# Revit family: FU_Stool_Sandler_VARYA Wood 4-2
name_source: partatom
category: Furniture
units: mm (PartAtom-declared; Revit-internal decimal feet)

## family parameters
Always vertical = No
Cut with Voids When Loaded = No
OmniClass Number = 23.21.23.15.17
Render Appearance Source = Family Geometry
Room Calculation Point = No
Shared = No
Work Plane-Based = Yes

## types (2) — shared parameters
401D = No
401G = No
BIMobject category = Chair
BIMobject category code = furniture-chair
BIMobject main category = Furniture
BIMobject main category code = furniture
Brand url = https://www.sandlerseating.com
Default Elevation = 1219.2 mm  [stored 4 ft]
Edition number = 1
IFC Classification = Furnishing Element
Manufacturer = Sandler
Manufacturer country = USA
Manufacturer name = Sandler
Masterformat 2014 Code = 12 48 43.13
Masterformat 2014 Description = Chair Mats
OmniClass Code = 23-21 23 15 17
Product Guid = ??
Product SKU = ??
Product data url = https://www.sandlerseating.com
Product family = Furniture
Product group = Chair
QR code = https://www.sandlerseating.com
Uniformat II Description = Movable Furnishings

## per-type parameters (varying)
| type | Depth | Description | Design country | Frame Material | Height | Shell Material | URL | width |
| VARYA 3.2 PP | 610 mm | Chair | Brasil | <By Category> | 1097.784 mm | <By Category> |  | 560 mm |
| VARYA Wood 4.2 | 430 mm  [stored 1.41076 ft] | Counterstool with a seat and back in beech or oak veneer on a steel sled base.
Greenguard Gold-certified to protect indoor air quality. |  | Epoxy - M1_B00 - Black | 910 mm | Wood - Oak - Natural - V | https://www.sandlerseating.com | 415 mm  [stored 1.36155 ft] |

note: column(s) folded — value = type name in every type: Model, Product name

note: [stored X ft] marks values corroborated as IEEE doubles in the binary element streams (Revit-internal decimal feet)

## geometry (parser evidence)
native form markers: Sweep x12
no freeform markers — native parametric forms only
